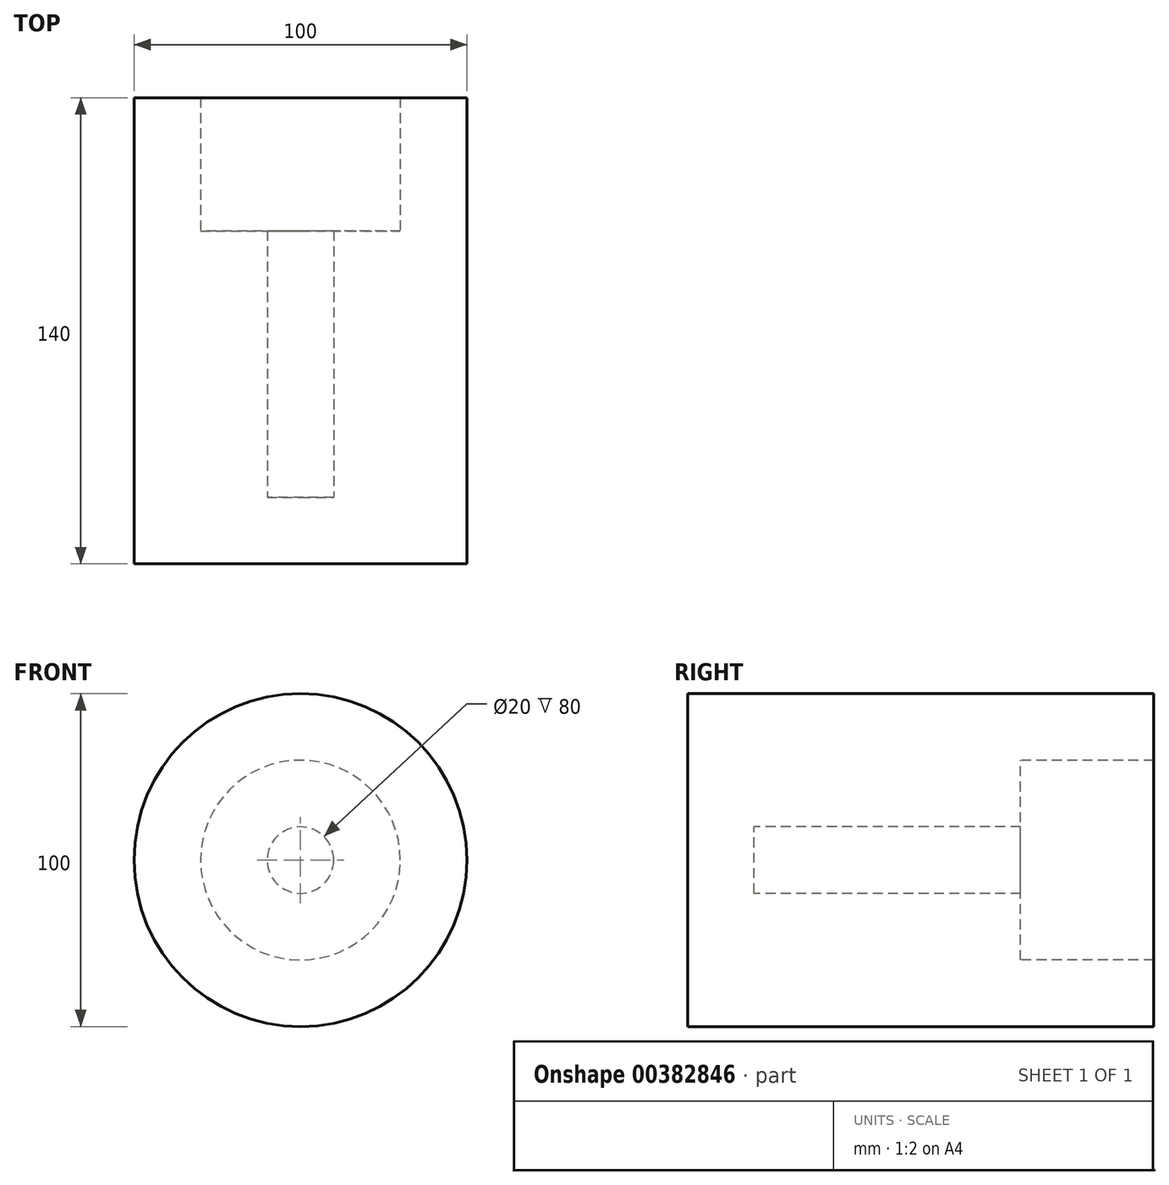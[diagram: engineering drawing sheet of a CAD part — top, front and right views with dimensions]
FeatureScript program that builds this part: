
annotation { "Feature Type Name" : "Feature", "Feature Type Description" : "" }
export const myFeature = defineFeature(function(context is Context, id is Id, definition is map)
    precondition{}
    {
        {
            var Q0;
            Q0=qCreatedBy(makeId("Right.planeOp"),FACE);
            var sketch = newSketch(context, id + "F0", { "sketchPlane" : qUnion([Q0])});
            skLineSegment(sketch, "E0.bottom", {"start": v(70, -50) * mm, "end": v(-70, -50) * mm});
            skLineSegment(sketch, "E0.top", {"start": v(70, 50) * mm, "end": v(-70, 50) * mm});
            skLineSegment(sketch, "E0.left", {"start": v(70, -50) * mm, "end": v(70, 50) * mm});
            skLineSegment(sketch, "E0.right", {"start": v(-70, -50) * mm, "end": v(-70, 50) * mm});
            skPoint(sketch, "E0.middle", {"position": v(0, 0) * mm});
            skLineSegment(sketch, "E1", {"start": v(-70, 0) * mm, "end": v(70, 0) * mm, "construction": true});
            skLineSegment(sketch, "E2.bottom", {"start": v(70, 30) * mm, "end": v(30, 30) * mm});
            skLineSegment(sketch, "E2.top", {"start": v(70, -30) * mm, "end": v(30, -30) * mm});
            skLineSegment(sketch, "E2.left", {"start": v(70, 30) * mm, "end": v(70, -30) * mm});
            skLineSegment(sketch, "E2.right", {"start": v(30, 30) * mm, "end": v(30, -30) * mm});
            skPoint(sketch, "E2.middle", {"position": v(50, 0) * mm});
            skLineSegment(sketch, "E3.bottom", {"start": v(30, 10) * mm, "end": v(-50, 10) * mm});
            skLineSegment(sketch, "E3.top", {"start": v(30, -10) * mm, "end": v(-50, -10) * mm});
            skLineSegment(sketch, "E3.left", {"start": v(30, 10) * mm, "end": v(30, -10) * mm});
            skLineSegment(sketch, "E3.right", {"start": v(-50, 10) * mm, "end": v(-50, -10) * mm});
            skPoint(sketch, "E3.middle", {"position": v(-10, 0) * mm});
            skLineSegment(sketch, "E4", {"start": v(-70, 0) * mm, "end": v(-50, 0) * mm});
            skSolve(sketch);
        }
        {
            var Q0;
            {var subQ1=sQuery(id+"F0.wireOp",EDGE,"E0.top");Q0=makeQuery(id+"F0.imprint","IMPRINT",FACE,{"disambiguationData":[TD([[makeQuery(id+"F0.imprint","IMPRINT",EDGE,{"derivedFrom":subQ1}),1.0]])]});}
            var Q1;
            Q1=sQuery(id+"F0.wireOp",EDGE,"E1");
            revolve(context, id + "F1", {"entities" : qUnion([Q0]), "axis" : qUnion([Q1]), "revolveType" : RevolveType.FULL});
        }
    });
